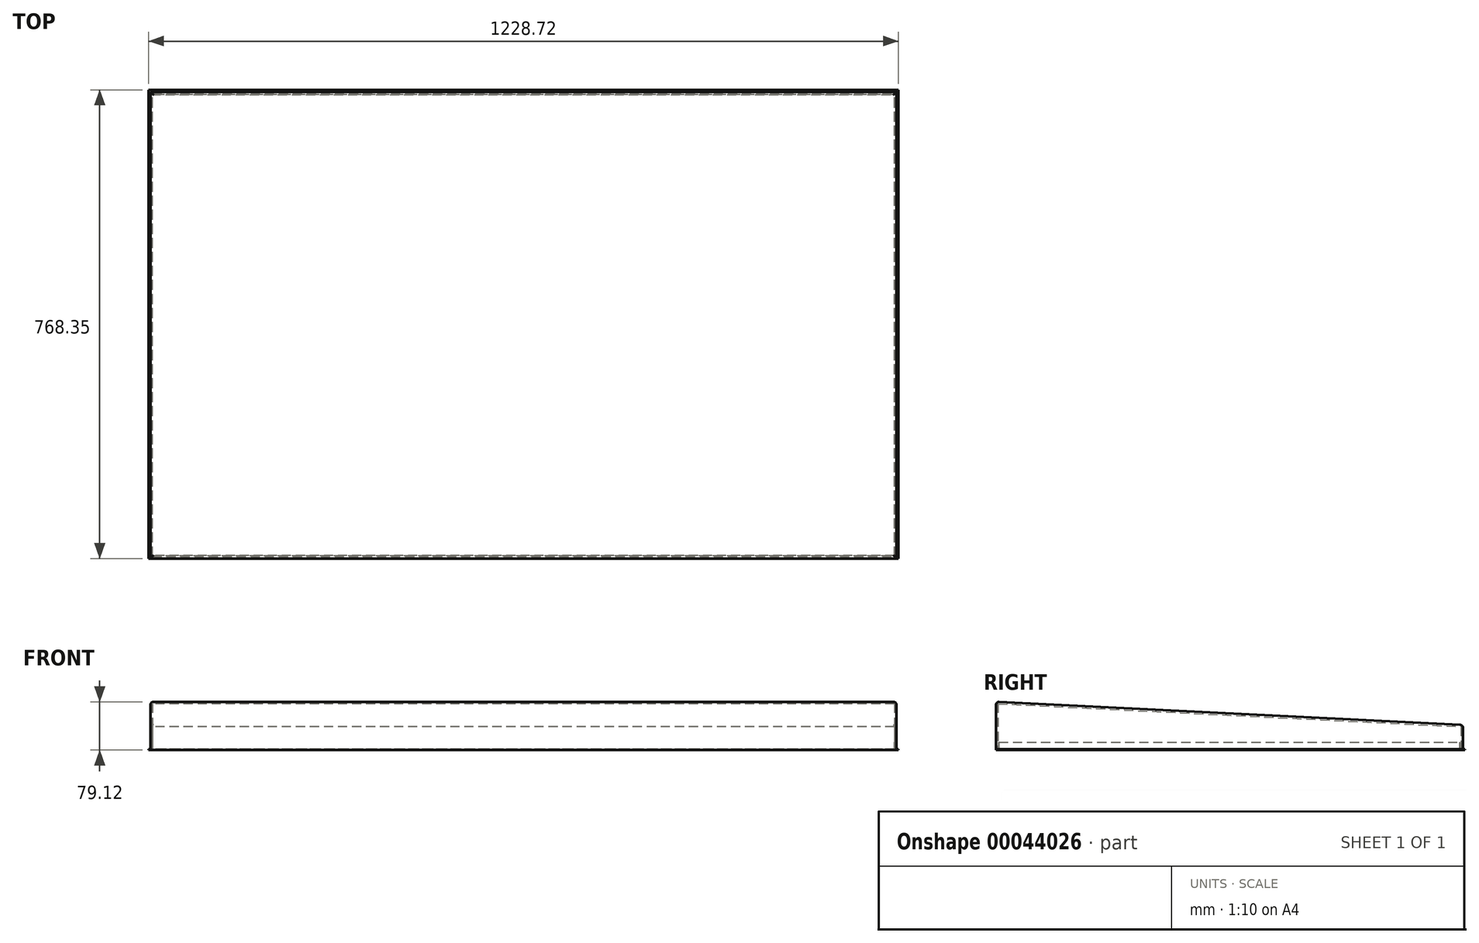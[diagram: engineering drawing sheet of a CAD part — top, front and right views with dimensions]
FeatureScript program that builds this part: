
annotation { "Feature Type Name" : "Feature", "Feature Type Description" : "" }
export const myFeature = defineFeature(function(context is Context, id is Id, definition is map)
    precondition{}
    {
        {
            var Q0;
            Q0=qCreatedBy(makeId("Top.planeOp"),FACE);
            var sketch = newSketch(context, id + "F0", { "sketchPlane" : qUnion([Q0])});
            skLineSegment(sketch, "E0.rect.bottom", {"start": v(611.19, 382.59) * mm, "end": v(-611.19, 382.59) * mm});
            skLineSegment(sketch, "E0.rect.top", {"start": v(611.19, -382.59) * mm, "end": v(-611.19, -382.59) * mm});
            skLineSegment(sketch, "E0.rect.left", {"start": v(611.19, 382.59) * mm, "end": v(611.19, -382.59) * mm});
            skLineSegment(sketch, "E0.rect.right", {"start": v(-611.19, 382.59) * mm, "end": v(-611.19, -382.59) * mm});
            skPoint(sketch, "E0.rect.middle", {"position": v(0, 0) * mm});
            skLineSegment(sketch, "E1.rect.bottom", {"start": v(-608.01, 379.41) * mm, "end": v(608.01, 379.41) * mm});
            skLineSegment(sketch, "E1.rect.top", {"start": v(-608.01, -379.41) * mm, "end": v(608.01, -379.41) * mm});
            skLineSegment(sketch, "E1.rect.left", {"start": v(-608.01, 379.41) * mm, "end": v(-608.01, -379.41) * mm});
            skLineSegment(sketch, "E1.rect.right", {"start": v(608.01, 379.41) * mm, "end": v(608.01, -379.41) * mm});
            skSolve(sketch);
        }
        {
            var Q0;
            Q0=makeQuery(id+"F0.imprint","IMPRINT",FACE,{"disambiguationData":[TD([[makeQuery(id+"F0.imprint","IMPRINT",EDGE,{"derivedFrom":sQuery(id+"F0.wireOp",EDGE,"E0.rect.bottom")}),1.0]])]});
            extrude(context, id + "F1", {"entities" : qUnion([Q0]), "depth" : 76.2 * mm});
        }
        {
            var Q0;
            Q0=makeQuery(id+"F1.opExtrude","SWEPT_FACE",FACE,{"disambiguationData":[OSD([sQuery(id+"F0.wireOp",EDGE,"E0.rect.left")])]});
            var sketch = newSketch(context, id + "F2", { "sketchPlane" : qUnion([Q0])});
            skLineSegment(sketch, "E2", {"start": v(-382.59, 76.2) * mm, "end": v(382.59, 38.1) * mm});
            skLineSegment(sketch, "E3", {"start": v(382.59, 38.1) * mm, "end": v(382.59, 76.2) * mm});
            skLineSegment(sketch, "E4", {"start": v(382.59, 76.2) * mm, "end": v(-382.59, 76.2) * mm});
            skSolve(sketch);
        }
        {
            var Q0;
            Q0 = qSketchRegion(id + "F2", true);
            extrude(context, id + "F3", {"entities" : qUnion([Q0]), "operationType" : NewBodyOperationType.REMOVE, "oppositeDirection" : true, "depth" : 1270 * mm});
        }
        {
            var Q0;
            Q0=makeQuery(id+"F3.boolean.opBoolean","COPY",FACE,{"derivedFrom":makeQuery(id+"F3.opExtrude","SWEPT_FACE",FACE,{"disambiguationData":[OSD([sQuery(id+"F2.wireOp",EDGE,"E2")])]})});
            var sketch = newSketch(context, id + "F4", { "sketchPlane" : qUnion([Q0])});
            skLineSegment(sketch, "E5", {"start": v(611.19, -385.9) * mm, "end": v(-611.19, -385.9) * mm});
            skLineSegment(sketch, "E6", {"start": v(-611.19, -385.9) * mm, "end": v(-611.19, 380.22) * mm});
            skLineSegment(sketch, "E7", {"start": v(-611.19, 380.22) * mm, "end": v(611.19, 380.22) * mm});
            skLineSegment(sketch, "E8", {"start": v(611.19, 380.22) * mm, "end": v(611.19, -385.9) * mm});
            skSolve(sketch);
        }
        {
            var Q0;
            Q0 = qSketchRegion(id + "F4", true);
            extrude(context, id + "F5", {"entities" : qUnion([Q0]), "operationType" : NewBodyOperationType.ADD, "depth" : 3.17 * mm});
        }
        {
            var Q0;
            Q0=qCreatedBy(makeId("Top.planeOp"),FACE);
            var sketch = newSketch(context, id + "F6", { "sketchPlane" : qUnion([Q0])});
            skLineSegment(sketch, "E9.bottom", {"start": v(-614.36, -382.59) * mm, "end": v(614.36, -382.59) * mm});
            skLineSegment(sketch, "E9.top", {"start": v(-614.36, 385.76) * mm, "end": v(614.36, 385.76) * mm});
            skLineSegment(sketch, "E9.left", {"start": v(-614.36, -382.59) * mm, "end": v(-614.36, 385.76) * mm});
            skLineSegment(sketch, "E9.right", {"start": v(614.36, -382.59) * mm, "end": v(614.36, 385.76) * mm});
            skSolve(sketch);
        }
        {
            var Q0;
            Q0 = qSketchRegion(id + "F6", true);
            extrude(context, id + "F7", {"entities" : qUnion([Q0]), "operationType" : NewBodyOperationType.ADD, "depth" : 1.59 * mm});
        }
        {
            var Q0;
            Q0=makeQuery(id+"F7.boolean.opBoolean","MERGE",FACE,{"derivedFrom":[makeQuery(id+"F1.opExtrude","CAP_FACE",FACE,{"disambiguationData":[OSD([sQuery(id+"F0.wireOp",EDGE,"E0.rect.bottom"),sQuery(id+"F0.wireOp",EDGE,"E0.rect.top"),sQuery(id+"F0.wireOp",EDGE,"E0.rect.left"),sQuery(id+"F0.wireOp",EDGE,"E0.rect.right"),sQuery(id+"F0.wireOp",EDGE,"E1.rect.bottom"),sQuery(id+"F0.wireOp",EDGE,"E1.rect.top"),sQuery(id+"F0.wireOp",EDGE,"E1.rect.left"),sQuery(id+"F0.wireOp",EDGE,"E1.rect.right")])],"isStart":true}),makeQuery(id+"F7.opExtrude","CAP_FACE",FACE,{"disambiguationData":[OSD([sQuery(id+"F6.wireOp",EDGE,"E9.bottom"),sQuery(id+"F6.wireOp",EDGE,"E9.top"),sQuery(id+"F6.wireOp",EDGE,"E9.left"),sQuery(id+"F6.wireOp",EDGE,"E9.right")])],"isStart":true})]});
            var sketch = newSketch(context, id + "F8", { "sketchPlane" : qUnion([Q0])});
            skLineSegment(sketch, "E10.rect.bottom", {"start": v(-609.6, 377.83) * mm, "end": v(609.6, 377.83) * mm});
            skLineSegment(sketch, "E10.rect.top", {"start": v(-609.6, -377.83) * mm, "end": v(609.6, -377.83) * mm});
            skLineSegment(sketch, "E10.rect.left", {"start": v(-609.6, 377.83) * mm, "end": v(-609.6, -377.83) * mm});
            skLineSegment(sketch, "E10.rect.right", {"start": v(609.6, 377.83) * mm, "end": v(609.6, -377.83) * mm});
            skPoint(sketch, "E10.rect.middle", {"position": v(0, 0) * mm});
            skSolve(sketch);
        }
        {
            var Q0;
            Q0 = qSketchRegion(id + "F8", true);
            extrude(context, id + "F9", {"entities" : qUnion([Q0]), "operationType" : NewBodyOperationType.REMOVE, "oppositeDirection" : true, "depth" : 12.7 * mm});
        }
        {
            var Q0;
            Q0=makeQuery(id+"F5.opExtrude","CAP_FACE",FACE,{"disambiguationData":[OSD([sQuery(id+"F4.wireOp",EDGE,"E5"),sQuery(id+"F4.wireOp",EDGE,"E6"),sQuery(id+"F4.wireOp",EDGE,"E7"),sQuery(id+"F4.wireOp",EDGE,"E8")])],"isStart":false});
            fillet(context, id + "F10", {"entities" : qUnion([Q0]), "radius" : 5.08 * mm, "tangentPropagation" : true, "allowEdgeOverflow" : false});
        }
    });
